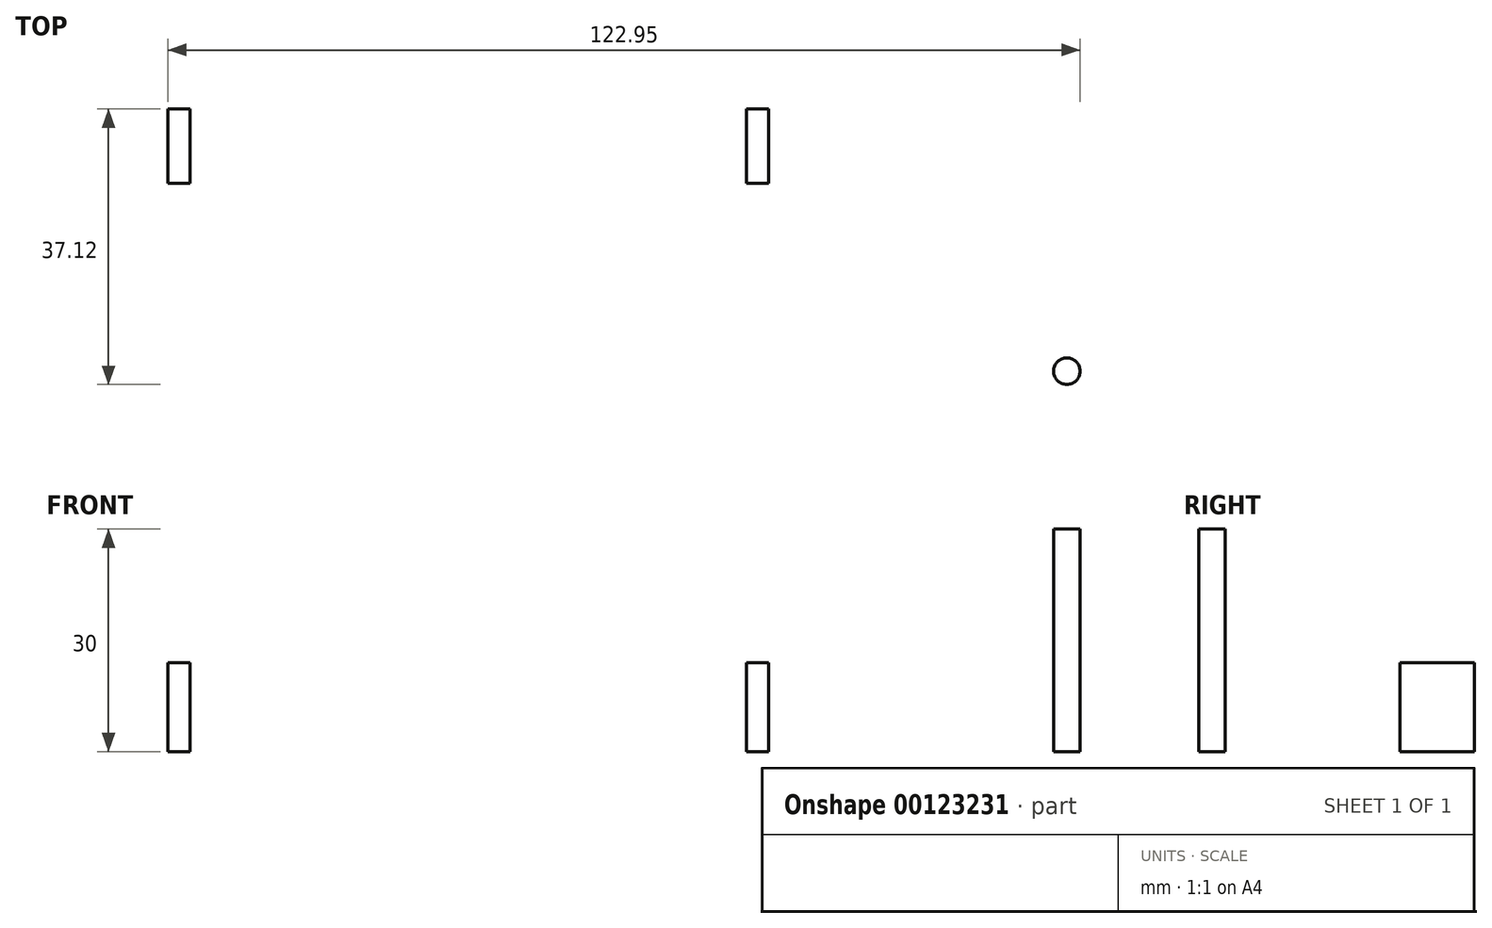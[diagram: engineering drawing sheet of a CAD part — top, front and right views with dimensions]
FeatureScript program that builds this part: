
annotation { "Feature Type Name" : "Feature", "Feature Type Description" : "" }
export const myFeature = defineFeature(function(context is Context, id is Id, definition is map)
    precondition{}
    {
        {
            var Q0;
            Q0=qCreatedBy(makeId("Top.planeOp"),FACE);
            var sketch = newSketch(context, id + "F0", { "sketchPlane" : qUnion([Q0])});
            skLineSegment(sketch, "E0.bottom", {"start": v(-50.38, 8.77) * mm, "end": v(14.62, 8.77) * mm});
            skLineSegment(sketch, "E0.top", {"start": v(-50.38, -26.8) * mm, "end": v(14.62, -26.8) * mm});
            skLineSegment(sketch, "E0.left", {"start": v(-60.38, -1.23) * mm, "end": v(-60.38, -16.8) * mm});
            skLineSegment(sketch, "E0.right", {"start": v(24.62, -1.23) * mm, "end": v(24.62, -16.8) * mm});
            skPoint(sketch, "E1.visualSharp", {"position": v(-60.38, 8.77) * mm});
            skArc(sketch, "E1.filletArc", {"start": v(-50.38, 8.77) * mm, "mid": v(-57.46, 5.84) * mm, "end": v(-60.38, -1.23) * mm});
            skPoint(sketch, "E2.visualSharp", {"position": v(24.62, 8.77) * mm});
            skArc(sketch, "E2.filletArc", {"start": v(24.62, -1.23) * mm, "mid": v(21.69, 5.84) * mm, "end": v(14.62, 8.77) * mm});
            skPoint(sketch, "E3.visualSharp", {"position": v(24.62, -26.8) * mm});
            skArc(sketch, "E3.filletArc", {"start": v(14.62, -26.8) * mm, "mid": v(21.69, -23.86) * mm, "end": v(24.62, -16.8) * mm});
            skPoint(sketch, "E4.visualSharp", {"position": v(-60.38, -26.8) * mm});
            skArc(sketch, "E4.filletArc", {"start": v(-60.38, -16.8) * mm, "mid": v(-57.46, -23.86) * mm, "end": v(-50.38, -26.8) * mm});
            skPoint(sketch, "E5", {"position": v(-34.77, 0) * mm});
            skPoint(sketch, "E6", {"position": v(-4.77, 0) * mm});
            skPoint(sketch, "E7", {"position": v(11.74, 0) * mm});
            skCircle(sketch, "E8", {"center": v(13.56, -9.37) * mm, "radius": 9.53 * mm});
            skSolve(sketch);
        }
        {
            var Q0;
            Q0=qCreatedBy(makeId("Top.planeOp"),FACE);
            cPlane(context, id + "F1", {"entities" : qUnion([Q0]), "cplaneType" : CPlaneType.OFFSET, "offset" : 10 * mm, "width" : 150 * mm, "height" : 150 * mm});
        }
        {
            var Q0;
            Q0=qCreatedBy(id+"F1.planeOp",FACE);
            var sketch = newSketch(context, id + "F2", { "sketchPlane" : qUnion([Q0])});
            skLineSegment(sketch, "E9.bottom", {"start": v(19.62, 7.64) * mm, "end": v(22.62, 7.64) * mm});
            skLineSegment(sketch, "E9.top", {"start": v(19.62, -2.36) * mm, "end": v(22.62, -2.36) * mm});
            skLineSegment(sketch, "E9.left", {"start": v(19.62, 7.64) * mm, "end": v(19.62, -2.36) * mm});
            skLineSegment(sketch, "E9.right", {"start": v(22.62, 7.64) * mm, "end": v(22.62, -2.36) * mm});
            skLineSegment(sketch, "E10.bottom", {"start": v(-58.38, 7.64) * mm, "end": v(-55.38, 7.64) * mm});
            skLineSegment(sketch, "E10.top", {"start": v(-58.38, -2.36) * mm, "end": v(-55.38, -2.36) * mm});
            skLineSegment(sketch, "E10.left", {"start": v(-58.38, 7.64) * mm, "end": v(-58.38, -2.36) * mm});
            skLineSegment(sketch, "E10.right", {"start": v(-55.38, 7.64) * mm, "end": v(-55.38, -2.36) * mm});
            skSolve(sketch);
        }
        {
            var Q0;
            Q0=qSketchRegion(id+"F2",true);
            extrude(context, id + "F3", {"entities" : qUnion([Q0]), "depth" : 12 * mm});
        }
        {
            var Q0;
            Q0=qCreatedBy(id+"F1.planeOp",FACE);
            var sketch = newSketch(context, id + "F4", { "sketchPlane" : qUnion([Q0])});
            skCircle(sketch, "E11", {"center": v(62.78, -27.7) * mm, "radius": 1.79 * mm});
            skSolve(sketch);
        }
        {
            var Q0;
            Q0=makeQuery(id+"F4.imprint","IMPRINT",FACE,{"disambiguationData":[TD([[makeQuery(id+"F4.imprint","IMPRINT",EDGE,{"derivedFrom":sQuery(id+"F4.wireOp",EDGE,"E11")}),1.0]])]});
            extrude(context, id + "F5", {"entities" : qUnion([Q0]), "depth" : 30 * mm});
        }
    });
